# Revit family: Gresham_OffcChrs_Bromley247
name_source: partatom
category: Furniture
units: mm (PartAtom-declared; Revit-internal decimal feet)

## family parameters
Always vertical = Yes
Cut with Voids When Loaded = No
OmniClass Number = 23.40.20.00
OmniClass Title = General Furniture and Specialties
Room Calculation Point = No
Shared = Yes
Work Plane-Based = No

## types (4) — shared parameters
AccessibilityPerformance = Height Adjustable
Assembly Code = E2020200
AssetType = Moveable
Category = Pr_40_50_12_57: Office chairs
CodePerformance = Exceeds level ‘S’ certification
Color = Black
Constituents = Upholstered seat, Upholstered back, Seat mechanism, Castors
DurationUnit = Years
ExpectedLife = 10
Features = Ideal for heavy duty use in Police, Security, Air Traffic Control rooms and other 24 hour working environments
Finish = Upholstery Back and Seat. Range of Upholstery Available
HighestSeatingHeight = 560 mm  [stored 1.83727 ft]
IfcExportAs = IfcFurnitureTypeEnum
IfcExportType = CHAIR
IsBuiltIn = No
Keynote = Pr_40_50_12_57
LowestSeatingHeight = 470 mm  [stored 1.54199 ft]
MainColor = Defined by material specified
Manufacturer = Gresham
ManufacturerName = Gresham Office Furniture
ManufacturerURL = https://gof.co.uk
Material = Upholstered CHRM Foam Seat, Optional Aluminium Base
NBSDescription = Office chairs
NBSReference = 45-35-20/330
Name = OfficeChairs_Bromley_Gresham
NominalLength = 680 mm  [stored 2.23097 ft]
ProductInformation = https://gof.co.uk
ReplacementCost = 0
Shape = Square
Style = Task Chair
URL = https://gof.co.uk
Uniclass2015Code = Pr_40_50_12_57
Uniclass2015Title = Office chairs
Uniclass2015Version = Pr-Products v1.10
WarrantyDurationLabor = 5
WarrantyDurationParts = 5
WarrantyDurationUnit = Years
zero-valued in all types: Cost, SeatingHeight

## per-type parameters (varying)
| type | BackType | Description | HasArms | Model | ModelNumber | ModelReference | NominalHeight | NominalWidth | Size | Type Comments |
| Task Upholstered Back | Nested_Gresham_OffcChrs_Bromley247_Back : Back | Task Chair with Upholstered Back | No | AX24/7 | AX24/7 | Task Chair with Upholstered Back | 1175 mm | 680 mm  [stored 2.23097 ft] | (H) 1175mm x (L) 680mm x (W) 680mm | Task Chair with Upholstered Back |
| Task Upholstered Back with Arms | Nested_Gresham_OffcChrs_Bromley247_Back : Back | Task Chair with Upholstered Back and Arms | Yes | AX24/7A22 | AX24/7A22 | Task Chair with Upholstered Back and Arms | 1175 mm | 705 mm  [stored 2.31299 ft] | (H) 1175mm x (L) 680mm x (W) 705mm | Task Chair with Upholstered Back and Arms |
| Task Upholstered Back with Headrest and Arms | Nested_Gresham_OffcChrs_Bromley247_Back : Back with Headrest | Task Upholstered Back with Headrest and Arms | Yes | AXR24/7A22 | AXR24/7A22 | Task Upholstered Back with Headrest and Arms | 1265 mm  [stored 4.15026 ft] | 705 mm  [stored 2.31299 ft] | (H) 1265mm x (L) 680mm x (W) 705mm | Task Upholstered Back with Headrest and Arms |
| Task Upholstered Back with Headrest | Nested_Gresham_OffcChrs_Bromley247_Back : Back with Headrest | Task Chair with Upholstered Back and Headrest | No | AXR24/7 | AXR24/7 | Task Chair with Upholstered Back and Headrest | 1265 mm  [stored 4.15026 ft] | 680 mm  [stored 2.23097 ft] | (H) 1265mm x (L) 680mm x (W) 680mm | Task Chair with Upholstered Back and Headrest |

note: [stored X ft] marks values corroborated as IEEE doubles in the binary element streams (Revit-internal decimal feet)

## geometry (parser evidence)
native form markers: Sweep x11
no freeform markers — native parametric forms only
